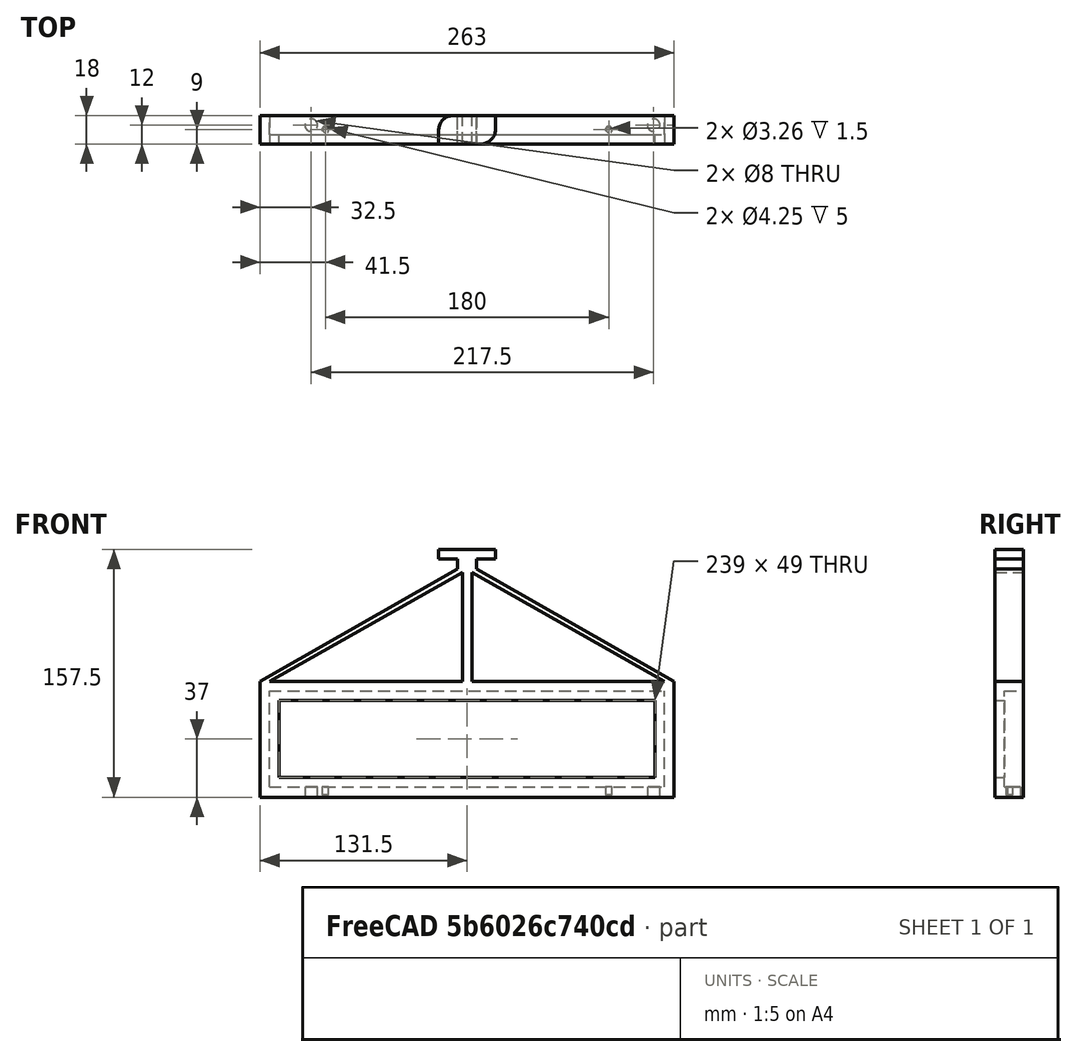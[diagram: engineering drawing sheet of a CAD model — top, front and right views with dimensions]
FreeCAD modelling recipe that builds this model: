
FCSTD DOCUMENT  (FreeCAD 0.20R2887)
Label: HiCoHolder
License: All rights reserved
LicenseURL: http://en.wikipedia.org/wiki/All_rights_reserved
objects: Part::Cylinder×8, Part::Box×7, Part::MultiFuse×3, Part::Wedge×2, Part::Cut×1
note: 21 computed .brp shape members not serialized (recipe doc carries the construction recipe); baked Part::Feature solids carry a one-line shape summary decoded from their .brp

FEATURE [Part::Box] Box  label="Cube"
  AttacherType = Attacher::AttachEngine3D
  Height = 73.5
  Length = 263
  Placement = pos=(0,0,-0.5) rot=(0,0,1;0rad)
  Width = 18
FEATURE [Part::Box] Box001  label="Cube001"
  AttacherType = Attacher::AttachEngine3D
  Height = 61
  Length = 251
  Placement = pos=(6,6,6) rot=(0,0,1;0rad)
  Width = 12
FEATURE [Part::Box] Box002  label="Cube002"
  AttacherType = Attacher::AttachEngine3D
  Height = 49
  Length = 239
  Placement = pos=(12,0,12) rot=(0,0,1;0rad)
  Width = 12
FEATURE [Part::Wedge] Wedge
  AttacherType = Attacher::AttachEngine3D
  Placement = pos=(0,18,73) rot=(1,0,0;1.5708rad)
  X2max = 131.5
  X2min = 131.5
  Xmax = 263
  Xmin = 0
  Ymax = 75
  Ymin = 0
  Z2max = 18
  Z2min = 0
  Zmax = 18
  Zmin = 0
FEATURE [Part::Wedge] Wedge001
  AttacherType = Attacher::AttachEngine3D
  Placement = pos=(0,18,73) rot=(1,0,0;1.5708rad)
  X2max = 131.5
  X2min = 131.5
  Xmax = 257
  Xmin = 6
  Ymax = 71
  Ymin = 0
  Z2max = 18
  Z2min = 0
  Zmax = 18
  Zmin = 0
FEATURE [Part::Box] Box003  label="Cube003"
  AttacherType = Attacher::AttachEngine3D
  Height = 75
  Length = 6
  Placement = pos=(128.5,0,73) rot=(0,0,1;0rad)
  Width = 18
FEATURE [Part::Box] Box004  label="Cube004"
  AttacherType = Attacher::AttachEngine3D
  Height = 6
  Length = 27
  Placement = pos=(113.5,0,151) rot=(0,0,1;0rad)
  Width = 9
  expr: .Placement.Base.x = 131.5 - 18
FEATURE [Part::Box] Box005  label="Cube005"
  AttacherType = Attacher::AttachEngine3D
  Height = 6
  Length = 27
  Placement = pos=(122.5,9,151) rot=(0,0,1;0rad)
  Width = 9
  expr: .Placement.Base.x = 131.5 - 13 + 4
FEATURE [Part::Cylinder] Cylinder
  Angle = 360
  AttacherType = Attacher::AttachEngine3D
  FirstAngle = 0
  Height = 6
  Placement = pos=(140.5,9,151) rot=(0,0,1;0rad)
  Radius = 9
  SecondAngle = 0
  expr: .Placement.Base.x = 131.5 + 9
FEATURE [Part::Cylinder] Cylinder001
  Angle = 360
  AttacherType = Attacher::AttachEngine3D
  FirstAngle = 0
  Height = 6
  Placement = pos=(122.5,9,151) rot=(0,0,1;0rad)
  Radius = 9
  SecondAngle = 0
  expr: .Placement.Base.x = 131.5 - 9
FEATURE [Part::Cylinder] Cylinder002
  Angle = 360
  AttacherType = Attacher::AttachEngine3D
  FirstAngle = 0
  Height = 8
  Placement = pos=(250,12,-0.5) rot=(0,0,1;0rad)
  Radius = 4
  SecondAngle = 0
FEATURE [Part::Cylinder] Cylinder003
  Angle = 360
  AttacherType = Attacher::AttachEngine3D
  FirstAngle = 0
  Height = 8
  Placement = pos=(32.5,12,-0.5) rot=(0,0,1;0rad)
  Radius = 4
  SecondAngle = 0
FEATURE [Part::Box] Box006  label="Cube006"
  AttacherType = Attacher::AttachEngine3D
  Height = 6.43
  Length = 12
  Placement = pos=(125.5,0,144.57) rot=(0,0,1;0rad)
  Width = 18
FEATURE [Part::Cylinder] Cylinder006
  Angle = 360
  AttacherType = Attacher::AttachEngine3D
  FirstAngle = 0
  Height = 5
  Placement = pos=(41.5,9,1) rot=(0,0,1;0rad)
  Radius = 2.125
  SecondAngle = 0
  expr: .Placement.Base.x = 131.5 - 90
FEATURE [Part::Cylinder] Cylinder004
  Angle = 360
  AttacherType = Attacher::AttachEngine3D
  FirstAngle = 0
  Height = 10
  Placement = pos=(41.5,9,-0.5) rot=(0,0,1;0rad)
  Radius = 1.63
  SecondAngle = 0
  expr: .Placement.Base.x = 131.5 - 90
FEATURE [Part::Cylinder] Cylinder007
  Angle = 360
  AttacherType = Attacher::AttachEngine3D
  FirstAngle = 0
  Height = 5
  Placement = pos=(221.5,9,1) rot=(0,0,1;0rad)
  Radius = 2.125
  SecondAngle = 0
  expr: .Placement.Base.x = 131.5 + 90
FEATURE [Part::Cylinder] Cylinder005
  Angle = 360
  AttacherType = Attacher::AttachEngine3D
  FirstAngle = 0
  Height = 10
  Placement = pos=(221.5,9,-0.5) rot=(0,0,1;0rad)
  Radius = 1.63
  SecondAngle = 0
  expr: .Placement.Base.x = 131.5 + 90
FEATURE [Part::MultiFuse] Fusion  label="Material"
  Shapes = -> [Box,Wedge]
FEATURE [Part::MultiFuse] Fusion001  label="Holes"
  Shapes = -> [Cylinder005,Cylinder004,Wedge001,Box001,Box002,Cylinder002,Cylinder003,Cylinder006,Cylinder007]
FEATURE [Part::Cut] Cut
  Base = -> Fusion
  Tool = -> Fusion001
FEATURE [Part::MultiFuse] Fusion002
  Shapes = -> [Box003,Box004,Box005,Cylinder,Cylinder001,Box006,Cut]
